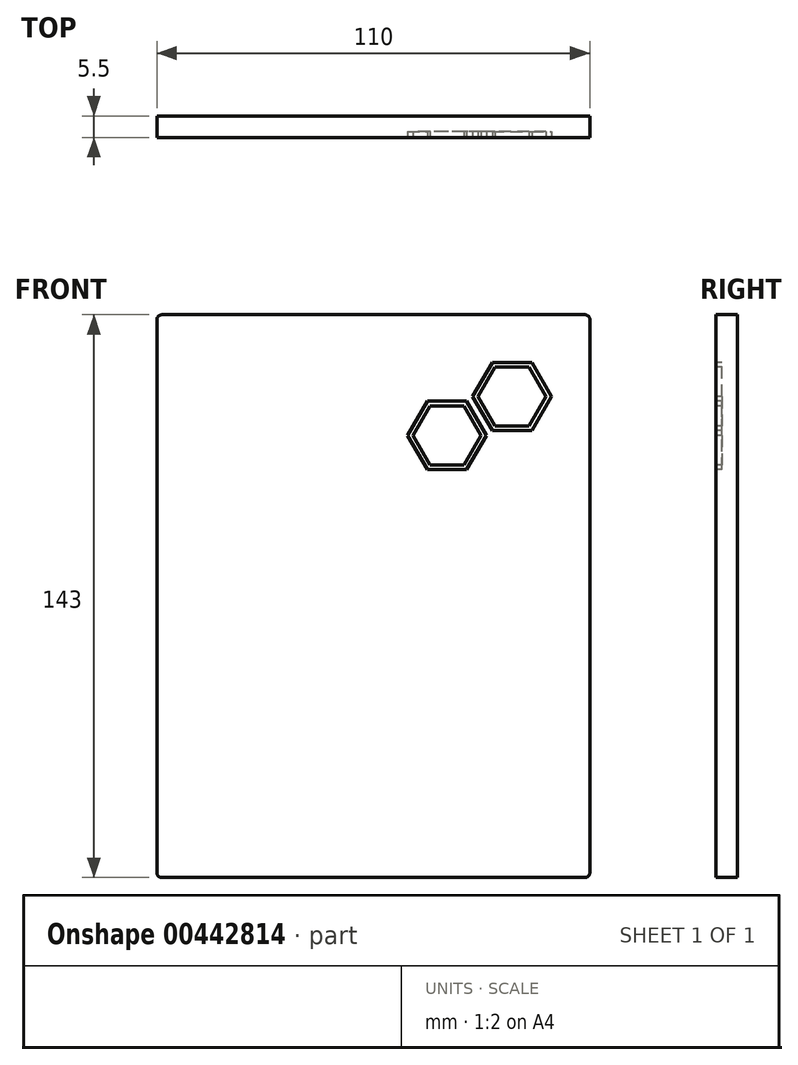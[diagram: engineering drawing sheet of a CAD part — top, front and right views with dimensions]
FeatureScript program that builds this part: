
annotation { "Feature Type Name" : "Feature", "Feature Type Description" : "" }
export const myFeature = defineFeature(function(context is Context, id is Id, definition is map)
    precondition{}
    {
        {
            var Q0;
            Q0=qCreatedBy(makeId("Front.planeOp"),FACE);
            var sketch = newSketch(context, id + "F0", { "sketchPlane" : qUnion([Q0])});
            skLineSegment(sketch, "E0.bottom", {"start": v(-1.27, 0) * mm, "end": v(-108.73, 0) * mm});
            skLineSegment(sketch, "E0.top", {"start": v(-1.27, 143) * mm, "end": v(-108.73, 143) * mm});
            skLineSegment(sketch, "E0.left", {"start": v(0, 1.27) * mm, "end": v(0, 141.73) * mm});
            skLineSegment(sketch, "E0.right", {"start": v(-110, 1.27) * mm, "end": v(-110, 141.73) * mm});
            skPoint(sketch, "E1.visualSharp", {"position": v(0, 143) * mm});
            skArc(sketch, "E1.filletArc", {"start": v(0, 141.73) * mm, "mid": v(-0.37, 142.63) * mm, "end": v(-1.27, 143) * mm});
            skPoint(sketch, "E2.visualSharp", {"position": v(-110, 143) * mm});
            skArc(sketch, "E2.filletArc", {"start": v(-108.73, 143) * mm, "mid": v(-109.63, 142.63) * mm, "end": v(-110, 141.73) * mm});
            skPoint(sketch, "E3.visualSharp", {"position": v(-110, 0) * mm});
            skArc(sketch, "E3.filletArc", {"start": v(-110, 1.27) * mm, "mid": v(-109.63, 0.37) * mm, "end": v(-108.73, 0) * mm});
            skPoint(sketch, "E4.visualSharp", {"position": v(0, 0) * mm});
            skArc(sketch, "E4.filletArc", {"start": v(-1.27, 0) * mm, "mid": v(-0.37, 0.37) * mm, "end": v(0, 1.27) * mm});
            skSolve(sketch);
        }
        {
            var Q0;
            Q0=qSketchRegion(id+"F0",true);
            extrude(context, id + "F1", {"entities" : qUnion([Q0]), "depth" : 5.5 * mm, "offsetDistance" : 25 * mm});
        }
        {
            var Q0;
            Q0=makeQuery(id+"F1.opExtrude","CAP_FACE",FACE,{"disambiguationData":[OSD([sQuery(id+"F0.wireOp",EDGE,"E0.bottom"),sQuery(id+"F0.wireOp",EDGE,"E0.top"),sQuery(id+"F0.wireOp",EDGE,"E0.left"),sQuery(id+"F0.wireOp",EDGE,"E0.right"),sQuery(id+"F0.wireOp",EDGE,"E1.filletArc"),sQuery(id+"F0.wireOp",EDGE,"E2.filletArc"),sQuery(id+"F0.wireOp",EDGE,"E3.filletArc"),sQuery(id+"F0.wireOp",EDGE,"E4.filletArc")])],"isStart":false});
            var sketch = newSketch(context, id + "F2", { "sketchPlane" : qUnion([Q0])});
            skCircle(sketch, "E5.cCircle", {"center": v(-19.76, 122.21) * mm, "radius": 8.66 * mm, "construction": true});
            skLineSegment(sketch, "E5.0", {"start": v(-14.76, 113.55) * mm, "end": v(-9.76, 122.21) * mm});
            skLineSegment(sketch, "E5.1", {"start": v(-24.76, 113.55) * mm, "end": v(-14.76, 113.55) * mm});
            skLineSegment(sketch, "E5.2", {"start": v(-29.76, 122.21) * mm, "end": v(-24.76, 113.55) * mm});
            skLineSegment(sketch, "E5.3", {"start": v(-24.76, 130.87) * mm, "end": v(-29.76, 122.21) * mm});
            skLineSegment(sketch, "E5.4", {"start": v(-14.76, 130.87) * mm, "end": v(-24.76, 130.87) * mm});
            skLineSegment(sketch, "E5.5", {"start": v(-9.76, 122.21) * mm, "end": v(-14.76, 130.87) * mm});
            skPoint(sketch, "E5.0.midPoint", {"position": v(-12.26, 117.88) * mm});
            skLineSegment(sketch, "E6.0", {"start": v(-15.43, 114.71) * mm, "end": v(-24.1, 114.71) * mm});
            skLineSegment(sketch, "E6.1", {"start": v(-24.1, 114.71) * mm, "end": v(-28.42, 122.21) * mm});
            skLineSegment(sketch, "E6.2", {"start": v(-28.42, 122.21) * mm, "end": v(-24.1, 129.71) * mm});
            skLineSegment(sketch, "E6.3", {"start": v(-24.1, 129.71) * mm, "end": v(-15.43, 129.71) * mm});
            skLineSegment(sketch, "E6.4", {"start": v(-15.43, 129.71) * mm, "end": v(-11.1, 122.21) * mm});
            skLineSegment(sketch, "E6.5", {"start": v(-11.1, 122.21) * mm, "end": v(-15.43, 114.71) * mm});
            skCircle(sketch, "E7.cCircle", {"center": v(-36.32, 112.36) * mm, "radius": 8.66 * mm, "construction": true});
            skLineSegment(sketch, "E7.0", {"start": v(-46.32, 112.36) * mm, "end": v(-41.32, 121.02) * mm});
            skLineSegment(sketch, "E7.1", {"start": v(-41.32, 121.02) * mm, "end": v(-31.32, 121.02) * mm});
            skLineSegment(sketch, "E7.2", {"start": v(-31.32, 121.02) * mm, "end": v(-26.32, 112.36) * mm});
            skLineSegment(sketch, "E7.3", {"start": v(-26.32, 112.36) * mm, "end": v(-31.32, 103.7) * mm});
            skLineSegment(sketch, "E7.4", {"start": v(-31.32, 103.7) * mm, "end": v(-41.32, 103.7) * mm});
            skLineSegment(sketch, "E7.5", {"start": v(-41.32, 103.7) * mm, "end": v(-46.32, 112.36) * mm});
            skPoint(sketch, "E7.0.midPoint", {"position": v(-43.82, 116.7) * mm});
            skLineSegment(sketch, "E8.0", {"start": v(-31.99, 104.86) * mm, "end": v(-40.65, 104.86) * mm});
            skLineSegment(sketch, "E8.1", {"start": v(-40.65, 104.86) * mm, "end": v(-44.98, 112.36) * mm});
            skLineSegment(sketch, "E8.2", {"start": v(-44.98, 112.36) * mm, "end": v(-40.65, 119.86) * mm});
            skLineSegment(sketch, "E8.3", {"start": v(-40.65, 119.86) * mm, "end": v(-31.99, 119.86) * mm});
            skLineSegment(sketch, "E8.4", {"start": v(-31.99, 119.86) * mm, "end": v(-27.65, 112.36) * mm});
            skLineSegment(sketch, "E8.5", {"start": v(-27.65, 112.36) * mm, "end": v(-31.99, 104.86) * mm});
            skLineSegment(sketch, "E9", {"start": v(-19.76, 122.21) * mm, "end": v(-19.76, 162.84) * mm, "construction": true});
            skSolve(sketch);
        }
        {
            var Q0;
            Q0 = qSketchRegion(id + "F2", true);
            extrude(context, id + "F3", {"entities" : qUnion([Q0]), "operationType" : NewBodyOperationType.REMOVE, "oppositeDirection" : true, "depth" : 1.5 * mm, "offsetDistance" : 25 * mm});
        }
    });
